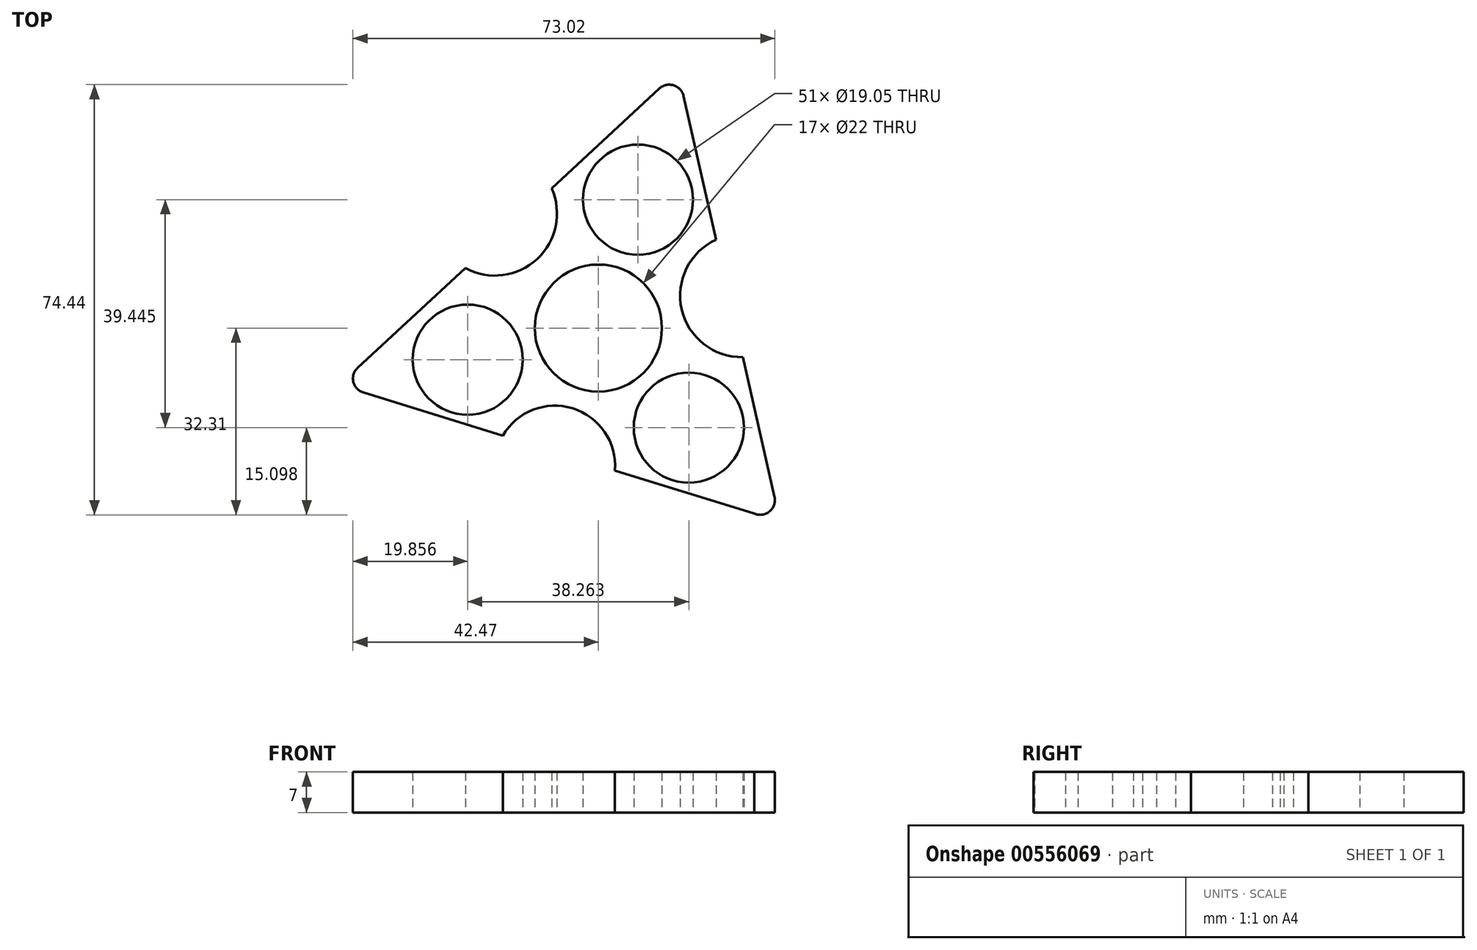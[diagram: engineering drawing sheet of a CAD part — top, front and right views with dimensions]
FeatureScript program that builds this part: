
annotation { "Feature Type Name" : "Feature", "Feature Type Description" : "" }
export const myFeature = defineFeature(function(context is Context, id is Id, definition is map)
    precondition{}
    {
        {
            var Q0;
            Q0=qCreatedBy(makeId("Top.planeOp"),FACE);
            var sketch = newSketch(context, id + "F0", { "sketchPlane" : qUnion([Q0])});
            skCircle(sketch, "E0", {"center": v(0, 0) * mm, "radius": 11 * mm});
            skCircle(sketch, "E1.cCircle", {"center": v(0, 0) * mm, "radius": 23.26 * mm, "construction": true});
            skLineSegment(sketch, "E1.0", {"start": v(14.74, 40.15) * mm, "end": v(30.48, -29.2) * mm});
            skLineSegment(sketch, "E1.2", {"start": v(-41.65, -6.86) * mm, "end": v(10.54, 41.45) * mm});
            skPoint(sketch, "E1.0.midPoint", {"position": v(22.69, 5.15) * mm});
            skCircle(sketch, "E2", {"center": v(15.65, -17.21) * mm, "radius": 9.53 * mm});
            skCircle(sketch, "E3", {"center": v(6.84, 22.23) * mm, "radius": 9.53 * mm});
            skCircle(sketch, "E4", {"center": v(-22.61, -5.45) * mm, "radius": 9.53 * mm});
            skPoint(sketch, "E5.visualSharp", {"position": v(13.77, 44.44) * mm});
            skArc(sketch, "E5.filletArc", {"start": v(14.74, 40.15) * mm, "mid": v(13.02, 42.01) * mm, "end": v(10.54, 41.45) * mm});
            skPoint(sketch, "E6.visualSharp", {"position": v(-45.37, -10.3) * mm});
            skArc(sketch, "E6.filletArc", {"start": v(-41.65, -6.86) * mm, "mid": v(-42.4, -9.28) * mm, "end": v(-40.68, -11.15) * mm});
            skPoint(sketch, "E7.visualSharp", {"position": v(31.6, -34.14) * mm});
            skArc(sketch, "E7.filletArc", {"start": v(26.99, -32.1) * mm, "mid": v(29.62, -31.73) * mm, "end": v(30.48, -29.2) * mm});
            skLineSegment(sketch, "E8", {"start": v(0, 0) * mm, "end": v(-15.56, 17.3) * mm});
            skLineSegment(sketch, "E9", {"start": v(0, 0) * mm, "end": v(22.69, 5.15) * mm});
            skLineSegment(sketch, "E10", {"start": v(-40.68, -11.15) * mm, "end": v(26.99, -32.1) * mm});
            skLineSegment(sketch, "E11", {"start": v(-40.68, -11.15) * mm, "end": v(-11.65, -20.13) * mm});
            skArc(sketch, "E12", {"start": v(-23.01, 10.4) * mm, "mid": v(-10.6, 11.94) * mm, "end": v(-8.1, 24.2) * mm});
            skArc(sketch, "E13", {"start": v(20.38, 15.3) * mm, "mid": v(14.4, 3.27) * mm, "end": v(25, -5.01) * mm});
            skArc(sketch, "E14", {"start": v(2.86, -24.63) * mm, "mid": v(-4.45, -13.89) * mm, "end": v(-16.55, -18.62) * mm});
            skLineSegment(sketch, "E15", {"start": v(0, 0) * mm, "end": v(-6.85, -21.62) * mm});
            skSolve(sketch);
        }
        {
            var Q0;
            Q0=makeQuery(id+"F0.imprint","IMPRINT",FACE,{"disambiguationData":[TD([[makeQuery(id+"F0.imprint","IMPRINT",EDGE,{"derivedFrom":sQuery(id+"F0.wireOp",EDGE,"E3")}),-1.0]])]});
            var Q1;
            Q1=makeQuery(id+"F0.imprint","IMPRINT",FACE,{"disambiguationData":[TD([[makeQuery(id+"F0.imprint","IMPRINT",EDGE,{"derivedFrom":sQuery(id+"F0.wireOp",EDGE,"E4")}),-1.0]])]});
            var Q2;
            Q2=makeQuery(id+"F0.imprint","IMPRINT",FACE,{"disambiguationData":[TD([[makeQuery(id+"F0.imprint","IMPRINT",EDGE,{"derivedFrom":sQuery(id+"F0.wireOp",EDGE,"E2")}),-1.0]])]});
            extrude(context, id + "F1", {"entities" : qUnion([Q0, Q1, Q2]), "depth" : 7 * mm, "offsetDistance" : 25.4 * mm});
        }
    });
